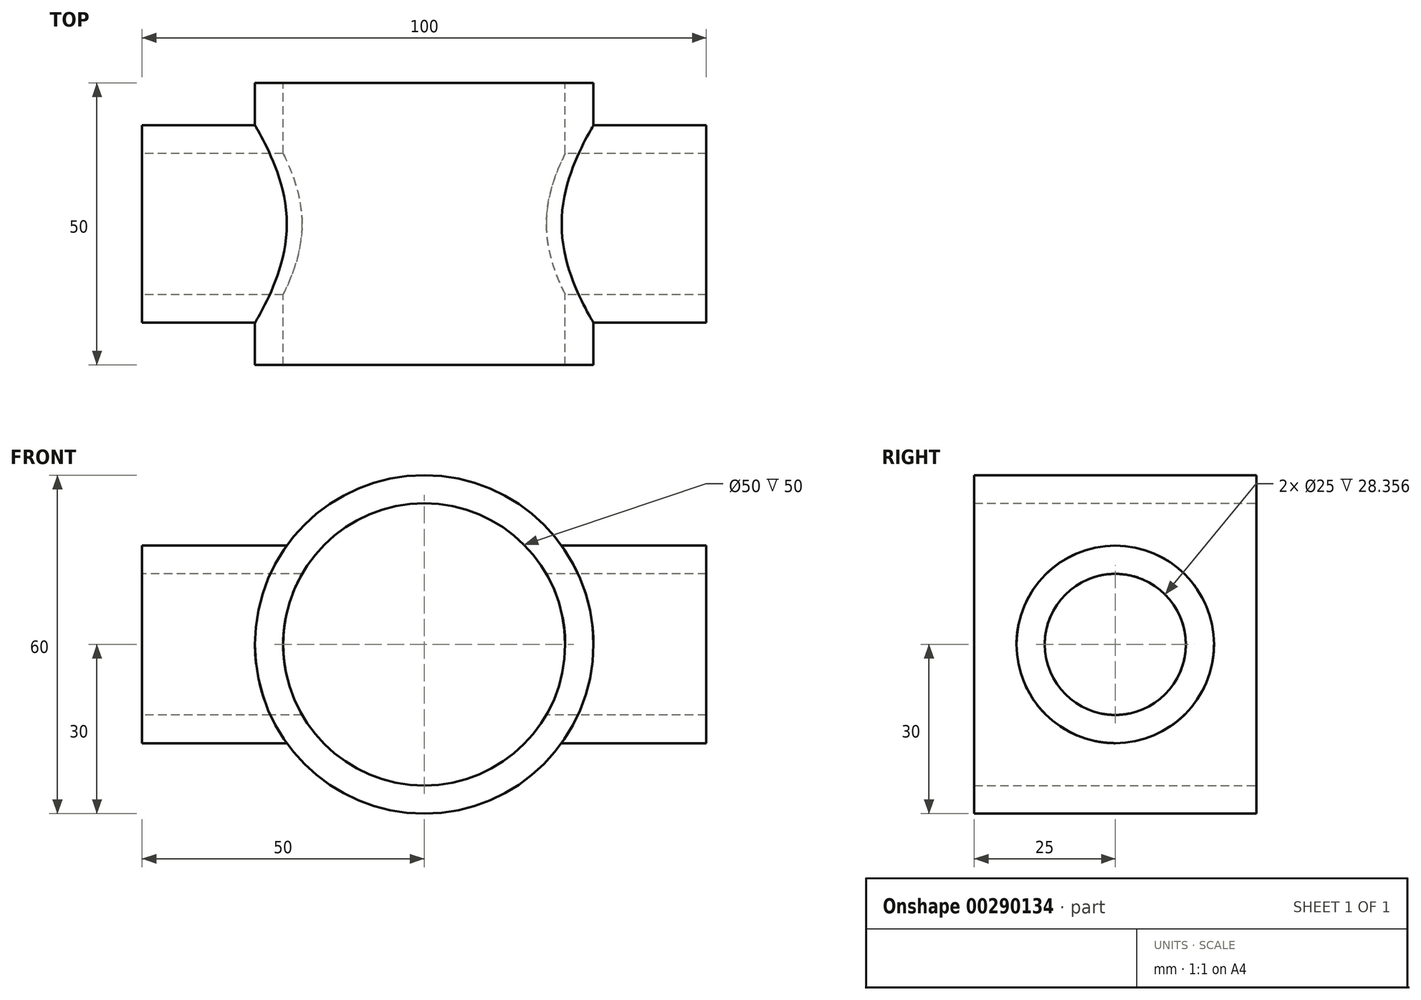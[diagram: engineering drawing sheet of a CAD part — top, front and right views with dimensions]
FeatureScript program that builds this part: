
annotation { "Feature Type Name" : "Feature", "Feature Type Description" : "" }
export const myFeature = defineFeature(function(context is Context, id is Id, definition is map)
    precondition{}
    {
        {
            var Q0;
            Q0=qCreatedBy(makeId("Front.planeOp"),FACE);
            var sketch = newSketch(context, id + "F0", { "sketchPlane" : qUnion([Q0])});
            skCircle(sketch, "E0", {"center": v(0, 0) * mm, "radius": 25 * mm});
            skCircle(sketch, "E1.0", {"center": v(0, 0) * mm, "radius": 30 * mm});
            skSolve(sketch);
        }
        {
            var Q0;
            Q0 = qSketchRegion(id + "F0", true);
            extrude(context, id + "F1", {"entities" : qUnion([Q0]), "depth" : 25 * mm, "hasSecondDirection" : true, "secondDirectionOppositeDirection" : true, "secondDirectionDepth" : 25 * mm});
        }
        {
            var Q0;
            Q0=qCreatedBy(makeId("Right.planeOp"),FACE);
            var sketch = newSketch(context, id + "F2", { "sketchPlane" : qUnion([Q0])});
            skCircle(sketch, "E2", {"center": v(0, 0) * mm, "radius": 12.5 * mm});
            skCircle(sketch, "E3.0", {"center": v(0, 0) * mm, "radius": 17.5 * mm});
            skSolve(sketch);
        }
        {
            var Q0;
            Q0 = qSketchRegion(id + "F2", true);
            extrude(context, id + "F3", {"entities" : qUnion([Q0]), "operationType" : NewBodyOperationType.ADD, "depth" : 50 * mm, "hasSecondDirection" : true, "secondDirectionOppositeDirection" : true, "secondDirectionDepth" : 50 * mm});
        }
        {
            var Q0;
            Q0=makeQuery(id+"F1.opExtrude","CAP_FACE",FACE,{"disambiguationData":[OSD([sQuery(id+"F0.wireOp",EDGE,"E0"),sQuery(id+"F0.wireOp",EDGE,"E1.0")])],"isStart":false});
            var sketch = newSketch(context, id + "F4", { "sketchPlane" : qUnion([Q0])});
            skCircle(sketch, "E4", {"center": v(0, 0) * mm, "radius": 25 * mm});
            skSolve(sketch);
        }
        {
            var Q0;
            Q0 = qSketchRegion(id + "F4", true);
            var Q1;
            Q1=makeQuery(id+"F1.opExtrude","CAP_FACE",FACE,{"disambiguationData":[OSD([sQuery(id+"F0.wireOp",EDGE,"E0"),sQuery(id+"F0.wireOp",EDGE,"E1.0")])],"isStart":true});
            extrude(context, id + "F5", {"entities" : qUnion([Q0]), "operationType" : NewBodyOperationType.REMOVE, "endBound" : BoundingType.UP_TO_SURFACE, "oppositeDirection" : true, "endBoundEntityFace" : qUnion([Q1]), "depth" : 25 * mm});
        }
        {
            var Q0;
            Q0=makeQuery(id+"F3.opExtrude","CAP_FACE",FACE,{"disambiguationData":[OSD([sQuery(id+"F2.wireOp",EDGE,"E2"),sQuery(id+"F2.wireOp",EDGE,"E3.0")])],"isStart":false});
            var sketch = newSketch(context, id + "F6", { "sketchPlane" : qUnion([Q0])});
            skCircle(sketch, "E5", {"center": v(0, 0) * mm, "radius": 12.5 * mm});
            skSolve(sketch);
        }
        {
            var Q0;
            Q0 = qSketchRegion(id + "F6", true);
            extrude(context, id + "F7", {"entities" : qUnion([Q0]), "operationType" : NewBodyOperationType.REMOVE, "endBound" : BoundingType.THROUGH_ALL, "oppositeDirection" : true, "depth" : 25 * mm});
        }
    });
